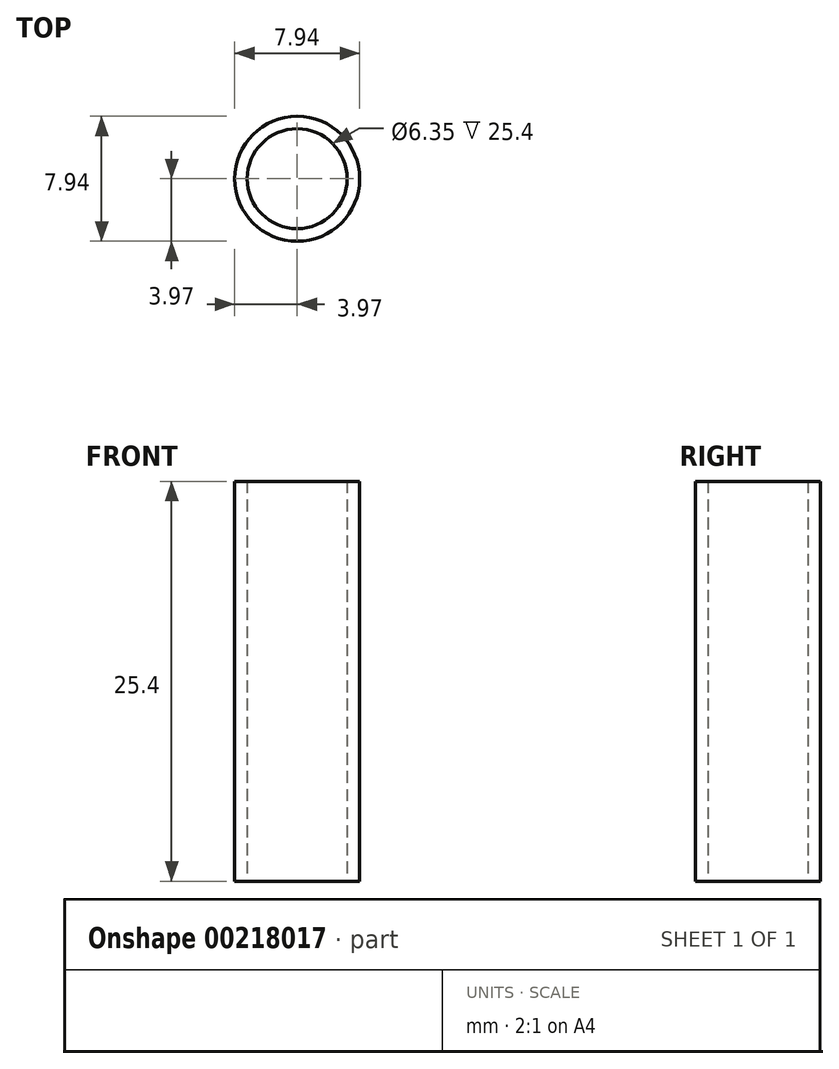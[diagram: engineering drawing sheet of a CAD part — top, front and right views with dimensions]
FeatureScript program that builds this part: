
annotation { "Feature Type Name" : "Feature", "Feature Type Description" : "" }
export const myFeature = defineFeature(function(context is Context, id is Id, definition is map)
    precondition{}
    {
        {
            var Q0;
            Q0=qCreatedBy(makeId("Top.planeOp"),FACE);
            var sketch = newSketch(context, id + "F0", { "sketchPlane" : qUnion([Q0])});
            skCircle(sketch, "E0", {"center": v(0, 0) * mm, "radius": 3.97 * mm});
            skCircle(sketch, "E1", {"center": v(0, 0) * mm, "radius": 3.18 * mm});
            skSolve(sketch);
        }
        {
            var Q0;
            Q0 = qSketchRegion(id + "F0", true);
            extrude(context, id + "F1", {"entities" : qUnion([Q0]), "depth" : 25.4 * mm, "offsetDistance" : 25.4 * mm});
        }
    });
